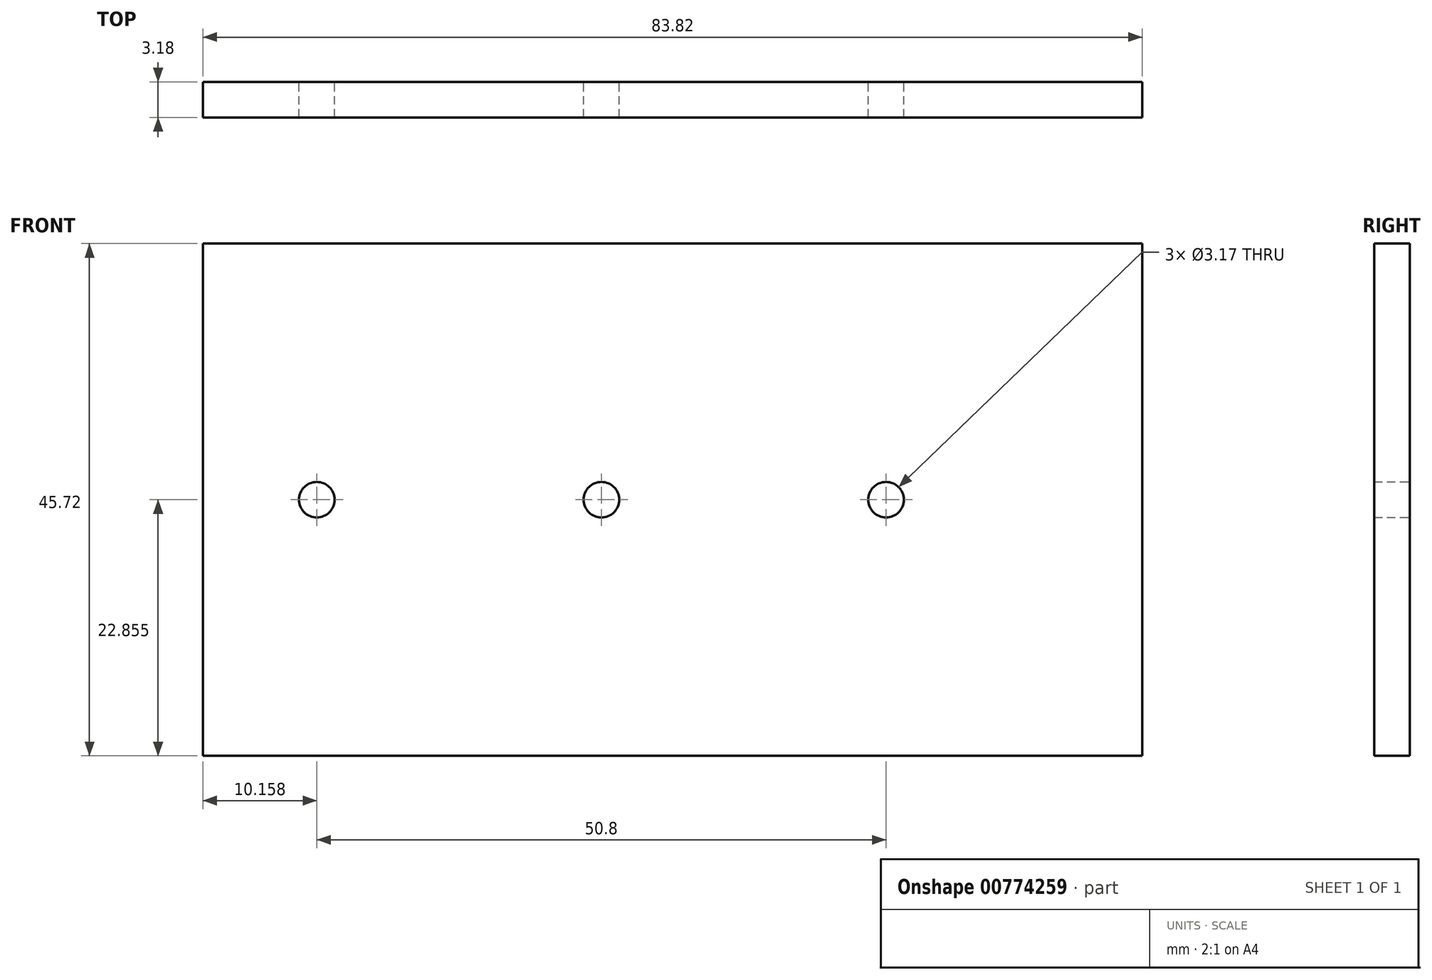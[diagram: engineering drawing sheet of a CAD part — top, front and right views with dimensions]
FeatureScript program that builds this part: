
annotation { "Feature Type Name" : "Feature", "Feature Type Description" : "" }
export const myFeature = defineFeature(function(context is Context, id is Id, definition is map)
    precondition{}
    {
        {
            var Q0;
            Q0=qCreatedBy(makeId("Front.planeOp"),FACE);
            var sketch = newSketch(context, id + "F0", { "sketchPlane" : qUnion([Q0])});
            skLineSegment(sketch, "E0.top", {"start": v(-1.5, -32.31) * mm, "end": v(74.7, -32.31) * mm});
            skLineSegment(sketch, "E0.right", {"start": v(74.7, 5.79) * mm, "end": v(74.7, -32.31) * mm});
            skPoint(sketch, "E1", {"position": v(4.85, -13.26) * mm});
            skPoint(sketch, "E2", {"position": v(11.2, -13.26) * mm});
            skPoint(sketch, "E3", {"position": v(-1.5, -13.26) * mm});
            skCircle(sketch, "E4", {"center": v(4.85, -13.26) * mm, "radius": 6.35 * mm});
            skPoint(sketch, "E5", {"position": v(30.25, -13.26) * mm});
            skCircle(sketch, "E6", {"center": v(30.25, -13.26) * mm, "radius": 19.05 * mm});
            skPoint(sketch, "E7", {"position": v(55.65, -13.26) * mm});
            skCircle(sketch, "E8", {"center": v(55.65, -13.26) * mm, "radius": 19.05 * mm});
            skCircle(sketch, "E9", {"center": v(30.25, -13.26) * mm, "radius": 6.35 * mm});
            skLineSegment(sketch, "E10", {"start": v(-1.5, 5.79) * mm, "end": v(-1.5, -32.31) * mm});
            skLineSegment(sketch, "E11.trimOffspring", {"start": v(-1.5, 5.79) * mm, "end": v(74.7, 5.79) * mm});
            skLineSegment(sketch, "E12.trimOffspring", {"start": v(-1.5, -13.26) * mm, "end": v(74.7, -13.26) * mm});
            skCircle(sketch, "E13", {"center": v(4.85, -13.26) * mm, "radius": 1.59 * mm});
            skCircle(sketch, "E14", {"center": v(30.25, -13.26) * mm, "radius": 1.59 * mm});
            skCircle(sketch, "E15", {"center": v(55.65, -13.26) * mm, "radius": 1.59 * mm});
            skLineSegment(sketch, "E16.top", {"start": v(-1.5, 9.6) * mm, "end": v(74.7, 9.6) * mm});
            skLineSegment(sketch, "E16.left", {"start": v(-1.5, 5.79) * mm, "end": v(-1.5, 9.6) * mm});
            skLineSegment(sketch, "E16.right", {"start": v(74.7, 5.79) * mm, "end": v(74.7, 9.6) * mm});
            skLineSegment(sketch, "E17.top", {"start": v(-1.5, -36.12) * mm, "end": v(74.7, -36.12) * mm});
            skLineSegment(sketch, "E17.left", {"start": v(-1.5, -32.31) * mm, "end": v(-1.5, -36.12) * mm});
            skLineSegment(sketch, "E17.right", {"start": v(74.7, -32.31) * mm, "end": v(74.7, -36.12) * mm});
            skLineSegment(sketch, "E18.bottom", {"start": v(-1.5, 9.6) * mm, "end": v(-5.31, 9.6) * mm});
            skLineSegment(sketch, "E18.top", {"start": v(-1.5, -36.12) * mm, "end": v(-5.31, -36.12) * mm});
            skLineSegment(sketch, "E18.left", {"start": v(-1.5, 9.6) * mm, "end": v(-1.5, -36.12) * mm});
            skLineSegment(sketch, "E18.right", {"start": v(-5.31, 9.6) * mm, "end": v(-5.31, -36.12) * mm});
            skLineSegment(sketch, "E19.bottom", {"start": v(74.7, 9.6) * mm, "end": v(78.5, 9.6) * mm});
            skLineSegment(sketch, "E19.top", {"start": v(74.7, -36.12) * mm, "end": v(78.5, -36.12) * mm});
            skLineSegment(sketch, "E19.left", {"start": v(74.7, 9.6) * mm, "end": v(74.7, -36.12) * mm});
            skLineSegment(sketch, "E19.right", {"start": v(78.5, 9.6) * mm, "end": v(78.5, -36.12) * mm});
            skSolve(sketch);
        }
        {
            var Q0;
            {var subQ0=sQuery(id+"F0.wireOp",EDGE,"E16.left");var subQ1=makeQuery(id+"F0.imprint","IMPRINT",EDGE,{"derivedFrom":subQ0});var subQ19=sQuery(id+"F0.wireOp",EDGE,"E16.right");var subQ20=makeQuery(id+"F0.imprint","IMPRINT",EDGE,{"derivedFrom":subQ19});Q0=qUnion([makeQuery(id+"F0.imprint","IMPRINT",FACE,{"disambiguationData":[TD([[makeQuery(id+"F0.imprint","IMPRINT",EDGE,{"derivedFrom":sQuery(id+"F0.wireOp",EDGE,"E16.top")}),-1.0]])]}),makeQuery(id+"F0.imprint","IMPRINT",FACE,{"disambiguationData":[TD([[subQ20,-1.0]])]}),makeQuery(id+"F0.imprint","IMPRINT",FACE,{"disambiguationData":[TD([[makeQuery(id+"F0.imprint","IMPRINT",EDGE,{"derivedFrom":sQuery(id+"F0.wireOp",EDGE,"E17.top")}),1.0]])]}),makeQuery(id+"F0.imprint","IMPRINT",FACE,{"disambiguationData":[TD([[subQ1,1.0]])]})]);}
            var Q1;
            {var subQ3=sQuery(id+"F0.wireOp",EDGE,"E8");var subQ5=sQuery(id+"F0.wireOp",EDGE,"E6");var subQ6=makeQuery(id+"F0.imprint","INTERSECT",VERTEX,{"disambiguationData":[OD(1.0)],"derivedFrom":[subQ5,subQ3]});Q1=makeQuery(id+"F0.imprint","IMPRINT",FACE,{"disambiguationData":[TD([[makeQuery(id+"F0.imprint","IMPRINT",EDGE,{"disambiguationData":[TD([[subQ6,-1.0]])],"derivedFrom":subQ5}),1.0]])]});}
            var Q2;
            {var subQ0=sQuery(id+"F0.wireOp",EDGE,"E12.trimOffspring");var subQ1=sQuery(id+"F0.wireOp",EDGE,"E9");var subQ2=makeQuery(id+"F0.imprint","INTERSECT",VERTEX,{"derivedFrom":[subQ1,subQ0]});Q2=makeQuery(id+"F0.imprint","IMPRINT",FACE,{"disambiguationData":[TD([[makeQuery(id+"F0.imprint","IMPRINT",EDGE,{"disambiguationData":[TD([[subQ2,-1.0]])],"derivedFrom":subQ0}),1.0]])]});}
            var Q3;
            {var subQ0=sQuery(id+"F0.wireOp",EDGE,"E12.trimOffspring");var subQ1=sQuery(id+"F0.wireOp",EDGE,"E9");var subQ2=makeQuery(id+"F0.imprint","INTERSECT",VERTEX,{"derivedFrom":[subQ1,subQ0]});Q3=makeQuery(id+"F0.imprint","IMPRINT",FACE,{"disambiguationData":[TD([[makeQuery(id+"F0.imprint","IMPRINT",EDGE,{"disambiguationData":[TD([[subQ2,-1.0]])],"derivedFrom":subQ0}),-1.0]])]});}
            var Q4;
            {var subQ5=sQuery(id+"F0.wireOp",EDGE,"E6");var subQ7=makeQuery(id+"F0.imprint","INTERSECT",VERTEX,{"derivedFrom":[sQuery(id+"F0.wireOp",EDGE,"E0.top"),subQ5]});Q4=makeQuery(id+"F0.imprint","IMPRINT",FACE,{"disambiguationData":[TD([[makeQuery(id+"F0.imprint","IMPRINT",EDGE,{"disambiguationData":[TD([[subQ7,-1.0]])],"derivedFrom":subQ5}),1.0]])]});}
            var Q5;
            {var subQ0=sQuery(id+"F0.wireOp",EDGE,"E8");var subQ1=sQuery(id+"F0.wireOp",EDGE,"E6");var subQ2=makeQuery(id+"F0.imprint","INTERSECT",VERTEX,{"disambiguationData":[OD(0.0)],"derivedFrom":[subQ1,subQ0]});Q5=makeQuery(id+"F0.imprint","IMPRINT",FACE,{"disambiguationData":[TD([[makeQuery(id+"F0.imprint","IMPRINT",EDGE,{"disambiguationData":[TD([[subQ2,-1.0]])],"derivedFrom":subQ1}),1.0]])]});}
            var Q6;
            {var subQ0=sQuery(id+"F0.wireOp",EDGE,"E12.trimOffspring");var subQ1=sQuery(id+"F0.wireOp",EDGE,"E6");var subQ2=makeQuery(id+"F0.imprint","INTERSECT",VERTEX,{"derivedFrom":[subQ1,subQ0]});Q6=makeQuery(id+"F0.imprint","IMPRINT",FACE,{"disambiguationData":[TD([[makeQuery(id+"F0.imprint","IMPRINT",EDGE,{"disambiguationData":[TD([[subQ2,-1.0]])],"derivedFrom":subQ1}),1.0]])]});}
            var Q7;
            {var subQ0=sQuery(id+"F0.wireOp",EDGE,"E8");var subQ1=sQuery(id+"F0.wireOp",EDGE,"E6");var subQ2=makeQuery(id+"F0.imprint","INTERSECT",VERTEX,{"disambiguationData":[OD(1.0)],"derivedFrom":[subQ1,subQ0]});Q7=makeQuery(id+"F0.imprint","IMPRINT",FACE,{"disambiguationData":[TD([[makeQuery(id+"F0.imprint","IMPRINT",EDGE,{"disambiguationData":[TD([[subQ2,-1.0]])],"derivedFrom":subQ1}),-1.0]])]});}
            var Q8;
            {var subQ0=sQuery(id+"F0.wireOp",EDGE,"E6");var subQ1=sQuery(id+"F0.wireOp",EDGE,"E0.top");var subQ2=makeQuery(id+"F0.imprint","INTERSECT",VERTEX,{"derivedFrom":[subQ1,subQ0]});Q8=makeQuery(id+"F0.imprint","IMPRINT",FACE,{"disambiguationData":[TD([[makeQuery(id+"F0.imprint","IMPRINT",EDGE,{"disambiguationData":[TD([[subQ2,-1.0]])],"derivedFrom":subQ1}),1.0]])]});}
            extrude(context, id + "F1", {"entities" : qUnion([Q0, Q1, Q2, Q3, Q4, Q5, Q6, Q7, Q8]), "depth" : 3.17 * mm, "offsetDistance" : 25.4 * mm});
        }
        {
            var Q0;
            {var subQ4=sQuery(id+"F0.wireOp",EDGE,"E6");var subQ6=sQuery(id+"F0.wireOp",EDGE,"E11.trimOffspring");var subQ7=makeQuery(id+"F0.imprint","INTERSECT",VERTEX,{"derivedFrom":[subQ4,subQ6]});Q0=makeQuery(id+"F0.imprint","IMPRINT",FACE,{"disambiguationData":[TD([[makeQuery(id+"F0.imprint","IMPRINT",EDGE,{"disambiguationData":[TD([[subQ7,-1.0]])],"derivedFrom":subQ4}),-1.0]])]});}
            var Q1;
            {var subQ0=sQuery(id+"F0.wireOp",EDGE,"E12.trimOffspring");var subQ4=sQuery(id+"F0.wireOp",EDGE,"E13");var subQ5=makeQuery(id+"F0.imprint","INTERSECT",VERTEX,{"disambiguationData":[OD(0.0)],"derivedFrom":[subQ0,subQ4]});Q1=makeQuery(id+"F0.imprint","IMPRINT",FACE,{"disambiguationData":[TD([[makeQuery(id+"F0.imprint","IMPRINT",EDGE,{"disambiguationData":[TD([[subQ5,-1.0]])],"derivedFrom":subQ4}),-1.0]])]});}
            var Q2;
            {var subQ0=sQuery(id+"F0.wireOp",EDGE,"E12.trimOffspring");var subQ4=sQuery(id+"F0.wireOp",EDGE,"E13");var subQ5=makeQuery(id+"F0.imprint","INTERSECT",VERTEX,{"disambiguationData":[OD(0.0)],"derivedFrom":[subQ0,subQ4]});Q2=makeQuery(id+"F0.imprint","IMPRINT",FACE,{"disambiguationData":[TD([[makeQuery(id+"F0.imprint","IMPRINT",EDGE,{"disambiguationData":[TD([[subQ5,1.0]])],"derivedFrom":subQ4}),-1.0]])]});}
            var Q3;
            {var subQ1=sQuery(id+"F0.wireOp",EDGE,"E0.top");var subQ3=sQuery(id+"F0.wireOp",EDGE,"E6");var subQ4=makeQuery(id+"F0.imprint","INTERSECT",VERTEX,{"derivedFrom":[subQ1,subQ3]});Q3=makeQuery(id+"F0.imprint","IMPRINT",FACE,{"disambiguationData":[TD([[makeQuery(id+"F0.imprint","IMPRINT",EDGE,{"disambiguationData":[TD([[subQ4,1.0]])],"derivedFrom":subQ1}),1.0]])]});}
            var Q4;
            {var subQ3=sQuery(id+"F0.wireOp",EDGE,"E8");var subQ6=sQuery(id+"F0.wireOp",EDGE,"E6");var subQ7=makeQuery(id+"F0.imprint","INTERSECT",VERTEX,{"disambiguationData":[OD(0.0)],"derivedFrom":[subQ6,subQ3]});Q4=makeQuery(id+"F0.imprint","IMPRINT",FACE,{"disambiguationData":[TD([[makeQuery(id+"F0.imprint","IMPRINT",EDGE,{"disambiguationData":[TD([[subQ7,-1.0]])],"derivedFrom":subQ6}),-1.0]])]});}
            var Q5;
            {var subQ1=sQuery(id+"F0.wireOp",EDGE,"E12.trimOffspring");var subQ5=sQuery(id+"F0.wireOp",EDGE,"E6");var subQ8=makeQuery(id+"F0.imprint","INTERSECT",VERTEX,{"derivedFrom":[subQ5,subQ1]});Q5=makeQuery(id+"F0.imprint","IMPRINT",FACE,{"disambiguationData":[TD([[makeQuery(id+"F0.imprint","IMPRINT",EDGE,{"disambiguationData":[TD([[subQ8,-1.0]])],"derivedFrom":subQ5}),-1.0]])]});}
            var Q6;
            {var subQ1=sQuery(id+"F0.wireOp",EDGE,"E0.top");var subQ3=sQuery(id+"F0.wireOp",EDGE,"E8");var subQ4=makeQuery(id+"F0.imprint","INTERSECT",VERTEX,{"derivedFrom":[subQ1,subQ3]});Q6=makeQuery(id+"F0.imprint","IMPRINT",FACE,{"disambiguationData":[TD([[makeQuery(id+"F0.imprint","IMPRINT",EDGE,{"disambiguationData":[TD([[subQ4,-1.0]])],"derivedFrom":subQ1}),1.0]])]});}
            var Q7;
            {var subQ0=sQuery(id+"F0.wireOp",EDGE,"E11.trimOffspring");var subQ3=sQuery(id+"F0.wireOp",EDGE,"E8");var subQ5=makeQuery(id+"F0.imprint","INTERSECT",VERTEX,{"derivedFrom":[subQ3,subQ0]});Q7=makeQuery(id+"F0.imprint","IMPRINT",FACE,{"disambiguationData":[TD([[makeQuery(id+"F0.imprint","IMPRINT",EDGE,{"disambiguationData":[TD([[subQ5,1.0]])],"derivedFrom":subQ3}),-1.0]])]});}
            extrude(context, id + "F2", {"entities" : qUnion([Q0, Q1, Q2, Q3, Q4, Q5, Q6, Q7]), "operationType" : NewBodyOperationType.ADD, "depth" : 3.17 * mm, "offsetDistance" : 25.4 * mm});
        }
    });
